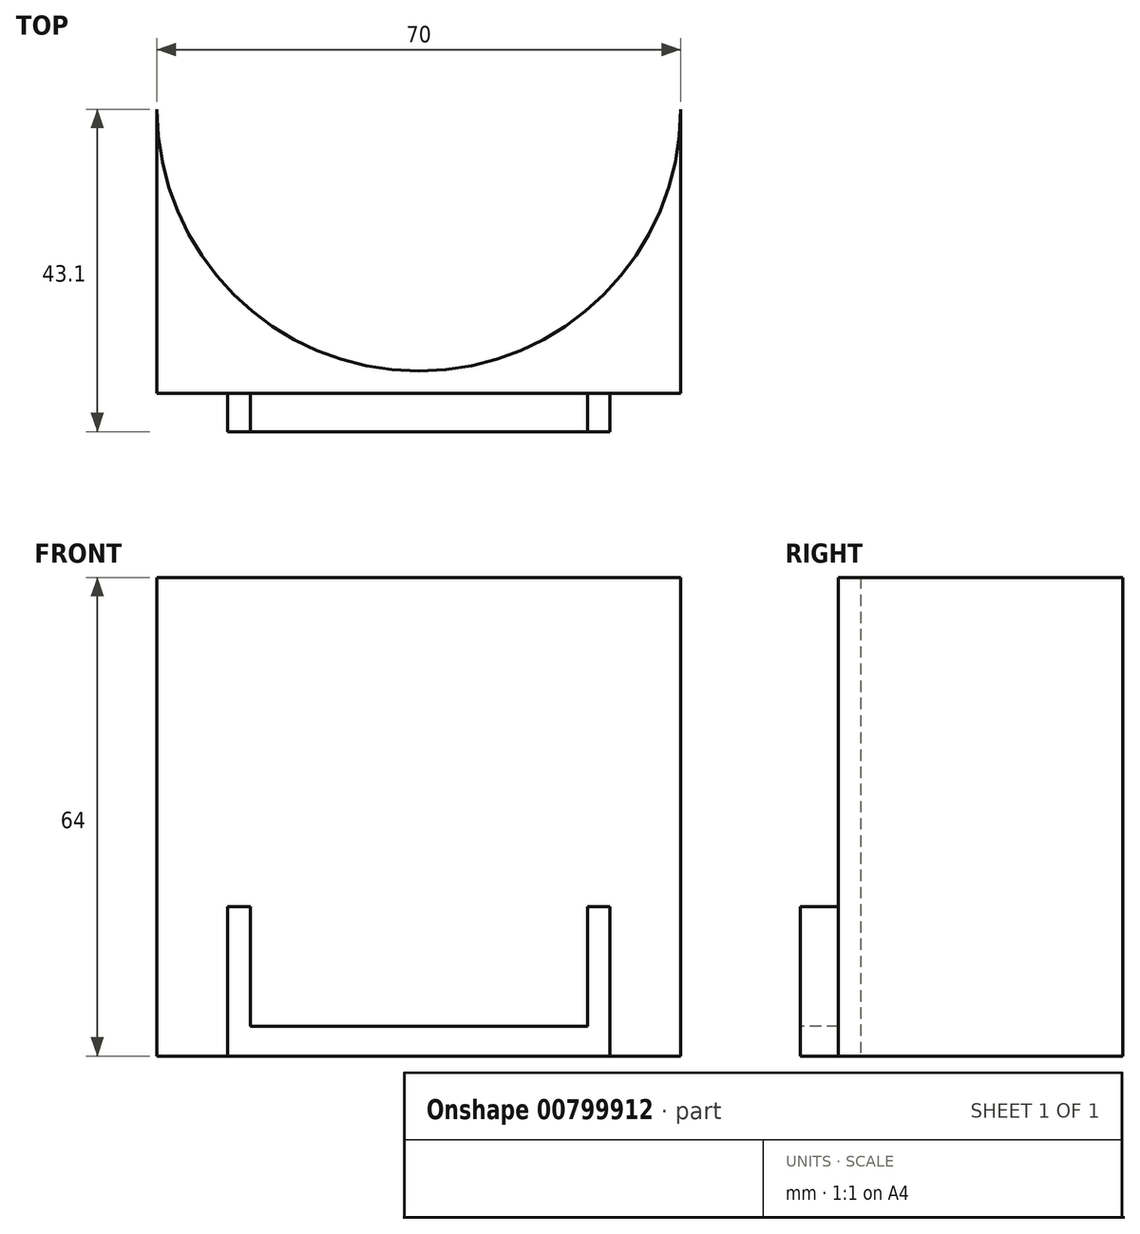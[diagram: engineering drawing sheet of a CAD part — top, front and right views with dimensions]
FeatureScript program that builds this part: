
annotation { "Feature Type Name" : "Feature", "Feature Type Description" : "" }
export const myFeature = defineFeature(function(context is Context, id is Id, definition is map)
    precondition{}
    {
        {
            var Q0;
            Q0=qCreatedBy(makeId("Top.planeOp"),FACE);
            var sketch = newSketch(context, id + "F0", { "sketchPlane" : qUnion([Q0])});
            skCircle(sketch, "E0", {"center": v(0, 0) * mm, "radius": 35 * mm});
            skLineSegment(sketch, "E1", {"start": v(0, -35) * mm, "end": v(0, -38) * mm});
            skLineSegment(sketch, "E2", {"start": v(-35, 0) * mm, "end": v(-35, -38) * mm});
            skLineSegment(sketch, "E3", {"start": v(35, 0) * mm, "end": v(35, -38) * mm});
            skLineSegment(sketch, "E4", {"start": v(35, -38) * mm, "end": v(0, -38) * mm});
            skLineSegment(sketch, "E5", {"start": v(-35, -38) * mm, "end": v(0, -38) * mm});
            skLineSegment(sketch, "E6", {"start": v(0, -38) * mm, "end": v(22.55, -38) * mm});
            skLineSegment(sketch, "E7", {"start": v(0, -38) * mm, "end": v(-22.55, -38) * mm});
            skLineSegment(sketch, "E8", {"start": v(-22.55, -38) * mm, "end": v(-22.55, -43.1) * mm});
            skLineSegment(sketch, "E9", {"start": v(-22.55, -43.1) * mm, "end": v(22.55, -43.1) * mm});
            skLineSegment(sketch, "E10", {"start": v(22.55, -43.1) * mm, "end": v(22.55, -38) * mm});
            skLineSegment(sketch, "E11", {"start": v(22.55, -43.1) * mm, "end": v(25.55, -43.1) * mm});
            skLineSegment(sketch, "E12", {"start": v(25.55, -43.1) * mm, "end": v(25.55, -38) * mm});
            skLineSegment(sketch, "E13", {"start": v(-22.55, -43.1) * mm, "end": v(-25.55, -43.1) * mm});
            skLineSegment(sketch, "E14", {"start": v(-25.55, -43.1) * mm, "end": v(-25.55, -38) * mm});
            skSolve(sketch);
        }
        {
            var Q0;
            {var subQ1=sQuery(id+"F0.wireOp",EDGE,"E1");Q0=makeQuery(id+"F0.imprint","IMPRINT",FACE,{"disambiguationData":[TD([[makeQuery(id+"F0.imprint","IMPRINT",EDGE,{"derivedFrom":subQ1}),-1.0]])]});}
            var Q1;
            {var subQ1=sQuery(id+"F0.wireOp",EDGE,"E1");Q1=makeQuery(id+"F0.imprint","IMPRINT",FACE,{"disambiguationData":[TD([[makeQuery(id+"F0.imprint","IMPRINT",EDGE,{"derivedFrom":subQ1}),1.0]])]});}
            extrude(context, id + "F1", {"entities" : qUnion([Q0, Q1]), "depth" : 64 * mm, "offsetDistance" : 25 * mm});
        }
        {
            var Q0;
            {var subQ0=sQuery(id+"F0.wireOp",EDGE,"E8");Q0=makeQuery(id+"F0.imprint","IMPRINT",FACE,{"disambiguationData":[TD([[makeQuery(id+"F0.imprint","IMPRINT",EDGE,{"derivedFrom":subQ0}),1.0]])]});}
            extrude(context, id + "F2", {"entities" : qUnion([Q0]), "operationType" : NewBodyOperationType.ADD, "depth" : 4 * mm, "offsetDistance" : 25 * mm});
        }
        {
            var Q0;
            {var subQ0=sQuery(id+"F0.wireOp",EDGE,"E8");Q0=makeQuery(id+"F0.imprint","IMPRINT",FACE,{"disambiguationData":[TD([[makeQuery(id+"F0.imprint","IMPRINT",EDGE,{"derivedFrom":subQ0}),-1.0]])]});}
            var Q1;
            {var subQ0=sQuery(id+"F0.wireOp",EDGE,"E10");Q1=makeQuery(id+"F0.imprint","IMPRINT",FACE,{"disambiguationData":[TD([[makeQuery(id+"F0.imprint","IMPRINT",EDGE,{"derivedFrom":subQ0}),-1.0]])]});}
            extrude(context, id + "F3", {"entities" : qUnion([Q0, Q1]), "operationType" : NewBodyOperationType.ADD, "depth" : 20 * mm, "offsetDistance" : 25 * mm});
        }
    });
